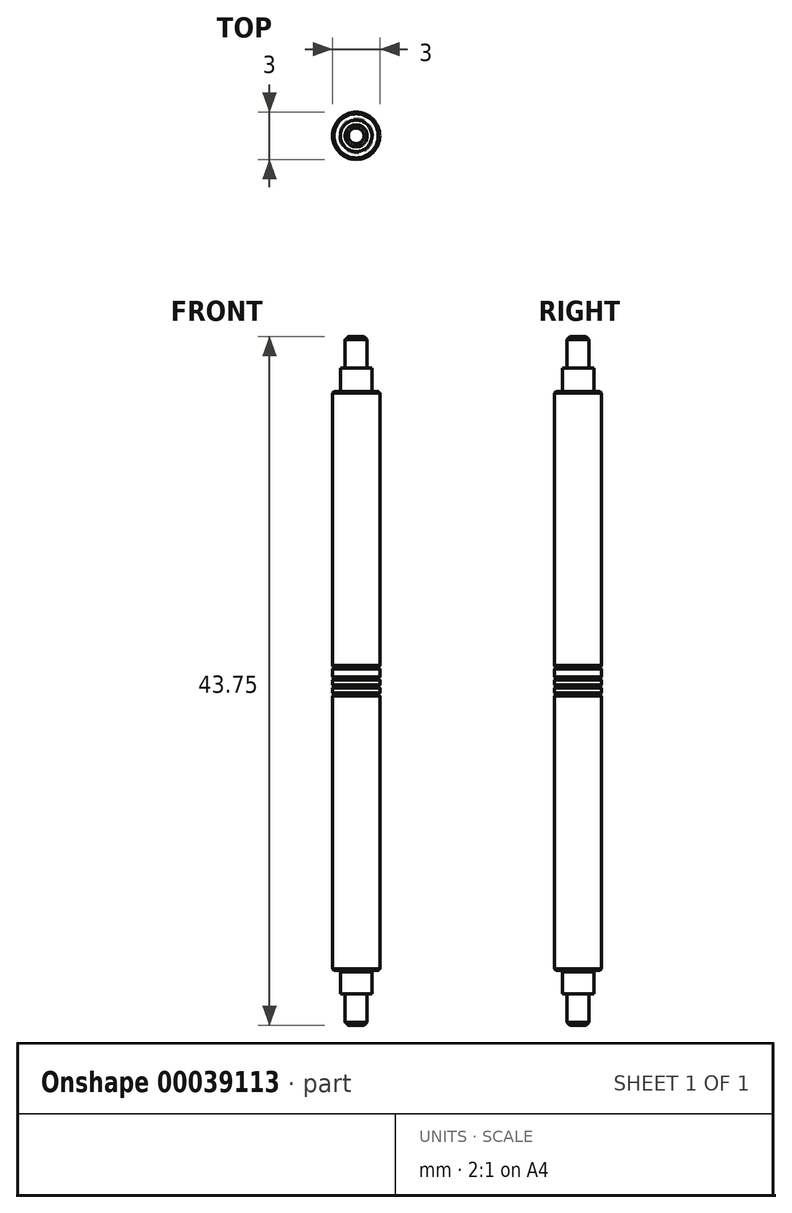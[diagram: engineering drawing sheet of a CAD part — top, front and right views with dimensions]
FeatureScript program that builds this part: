
annotation { "Feature Type Name" : "Feature", "Feature Type Description" : "" }
export const myFeature = defineFeature(function(context is Context, id is Id, definition is map)
    precondition{}
    {
        {
            var Q0;
            Q0=qCreatedBy(makeId("Front.planeOp"),FACE);
            var sketch = newSketch(context, id + "F0", { "sketchPlane" : qUnion([Q0])});
            skLineSegment(sketch, "E0.bottom", {"start": v(0, 36.75) * mm, "end": v(1.5, 36.75) * mm});
            skLineSegment(sketch, "E0.top", {"start": v(0, 0) * mm, "end": v(1.5, 0) * mm});
            skLineSegment(sketch, "E0.right", {"start": v(1.5, 36.75) * mm, "end": v(1.5, 19.33) * mm});
            skLineSegment(sketch, "E1.bottom", {"start": v(1, 0) * mm, "end": v(0, 0) * mm});
            skLineSegment(sketch, "E1.top", {"start": v(1, -1.5) * mm, "end": v(0, -1.5) * mm});
            skLineSegment(sketch, "E1.left", {"start": v(1, 0) * mm, "end": v(1, -1.5) * mm});
            skLineSegment(sketch, "E2.bottom", {"start": v(0.7, -1.5) * mm, "end": v(0, -1.5) * mm});
            skLineSegment(sketch, "E2.top", {"start": v(0.7, -3.5) * mm, "end": v(0, -3.5) * mm});
            skLineSegment(sketch, "E2.left", {"start": v(0.7, -1.5) * mm, "end": v(0.7, -3.5) * mm});
            skLineSegment(sketch, "E3.bottom", {"start": v(1, 36.75) * mm, "end": v(0, 36.75) * mm});
            skLineSegment(sketch, "E3.top", {"start": v(1, 38.25) * mm, "end": v(0, 38.25) * mm});
            skLineSegment(sketch, "E3.left", {"start": v(1, 36.75) * mm, "end": v(1, 38.25) * mm});
            skLineSegment(sketch, "E4.bottom", {"start": v(0.7, 38.25) * mm, "end": v(0, 38.25) * mm});
            skLineSegment(sketch, "E4.top", {"start": v(0.7, 40.25) * mm, "end": v(0, 40.25) * mm});
            skLineSegment(sketch, "E4.left", {"start": v(0.7, 38.25) * mm, "end": v(0.7, 40.25) * mm});
            skPoint(sketch, "E5", {"position": v(0, -3.5) * mm});
            skPoint(sketch, "E6", {"position": v(0, -1.5) * mm});
            skPoint(sketch, "E7", {"position": v(0, 40.25) * mm});
            skPoint(sketch, "E8", {"position": v(0, 38.25) * mm});
            skPoint(sketch, "E9", {"position": v(0, 36.75) * mm});
            skLineSegment(sketch, "E10", {"start": v(0, 40.25) * mm, "end": v(0, 38.25) * mm});
            skLineSegment(sketch, "E11", {"start": v(0, 38.25) * mm, "end": v(0, 36.75) * mm});
            skLineSegment(sketch, "E12", {"start": v(0, 36.75) * mm, "end": v(0, 0) * mm});
            skLineSegment(sketch, "E13", {"start": v(0, 0) * mm, "end": v(0, -3.5) * mm});
            skLineSegment(sketch, "E14", {"start": v(1.5, 17.43) * mm, "end": v(1.4, 17.53) * mm});
            skLineSegment(sketch, "E15", {"start": v(1.4, 17.52) * mm, "end": v(1.5, 17.62) * mm});
            skLineSegment(sketch, "E16", {"start": v(1.5, 17.93) * mm, "end": v(1.4, 18.03) * mm});
            skLineSegment(sketch, "E17", {"start": v(1.4, 18.03) * mm, "end": v(1.5, 18.13) * mm});
            skLineSegment(sketch, "E18", {"start": v(1.5, 18.43) * mm, "end": v(1.4, 18.53) * mm});
            skLineSegment(sketch, "E19", {"start": v(1.4, 18.53) * mm, "end": v(1.5, 18.63) * mm});
            skLineSegment(sketch, "E20", {"start": v(1.5, 19.13) * mm, "end": v(1.4, 19.23) * mm});
            skLineSegment(sketch, "E21", {"start": v(1.4, 19.23) * mm, "end": v(1.5, 19.33) * mm});
            skLineSegment(sketch, "E22.trimOffspring", {"start": v(1.5, 17.43) * mm, "end": v(1.5, 0) * mm});
            skLineSegment(sketch, "E23.trimOffspring", {"start": v(1.5, 17.93) * mm, "end": v(1.5, 17.62) * mm});
            skLineSegment(sketch, "E24.trimOffspring", {"start": v(1.5, 18.43) * mm, "end": v(1.5, 18.13) * mm});
            skLineSegment(sketch, "E25.trimOffspring", {"start": v(1.5, 19.13) * mm, "end": v(1.5, 18.63) * mm});
            skSolve(sketch);
        }
        {
            var Q0;
            Q0 = qSketchRegion(id + "F0", true);
            var Q1;
            Q1=sQuery(id+"F0.wireOp",EDGE,"E12");
            revolve(context, id + "F1", {"entities" : qUnion([Q0]), "axis" : qUnion([Q1]), "revolveType" : RevolveType.FULL});
        }
        {
            var Q0;
            Q0=makeQuery(id+"F1.opRevolve","SWEPT_EDGE",EDGE,{"disambiguationData":[OSD([sQuery(id+"F0.wireOp",EDGE,"E4.top"),sQuery(id+"F0.wireOp",EDGE,"E4.left")])]});
            chamfer(context, id + "F2", {"entities" : qUnion([Q0]), "chamferType" : ChamferType.OFFSET_ANGLE, "width" : 0.2 * mm, "oppositeDirection" : false, "angle" : 45 * degree, "tangentPropagation" : true});
        }
        {
            var Q0;
            Q0=makeQuery(id+"F1.opRevolve","SWEPT_EDGE",EDGE,{"disambiguationData":[OSD([sQuery(id+"F0.wireOp",EDGE,"E0.bottom"),sQuery(id+"F0.wireOp",EDGE,"E0.right")])]});
            chamfer(context, id + "F3", {"entities" : qUnion([Q0]), "chamferType" : ChamferType.OFFSET_ANGLE, "width" : 0.1 * mm, "oppositeDirection" : false, "angle" : 45 * degree, "tangentPropagation" : true});
        }
        {
            var Q0;
            Q0=makeQuery(id+"F1.opRevolve","SWEPT_EDGE",EDGE,{"disambiguationData":[OSD([sQuery(id+"F0.wireOp",EDGE,"E2.top"),sQuery(id+"F0.wireOp",EDGE,"E2.left")])]});
            chamfer(context, id + "F4", {"entities" : qUnion([Q0]), "chamferType" : ChamferType.OFFSET_ANGLE, "width" : 0.2 * mm, "oppositeDirection" : false, "angle" : 45 * degree, "tangentPropagation" : true});
        }
        {
            var Q0;
            Q0=makeQuery(id+"F1.opRevolve","SWEPT_EDGE",EDGE,{"disambiguationData":[OSD([sQuery(id+"F0.wireOp",EDGE,"E0.top"),sQuery(id+"F0.wireOp",EDGE,"E0.right")])]});
            chamfer(context, id + "F5", {"entities" : qUnion([Q0]), "chamferType" : ChamferType.OFFSET_ANGLE, "width" : 0.1 * mm, "oppositeDirection" : false, "angle" : 45 * degree, "tangentPropagation" : true});
        }
    });
